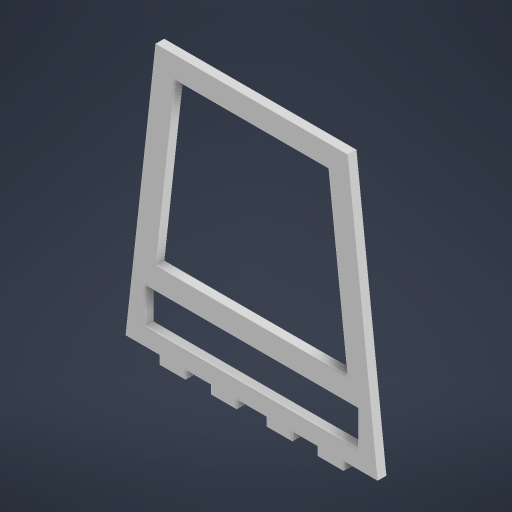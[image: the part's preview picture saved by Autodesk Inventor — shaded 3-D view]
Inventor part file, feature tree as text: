
AUTODESK INVENTOR PART (.ipt)
format: ipt  version: 2023.2 (Build 272271000, 271)  size: 279,040 bytes
history: native  units: mm
features: sketch x2
ambient origin geometry x8: Origin, YZ Plane, XZ Plane, XY Plane, X Axis, Y Axis, Z Axis, Center Point
bodies: Body1 (feature_tree)
feature tree (2):
  sketch  "Sketch1"  dims[d229=90.0mm]
  sketch  "Sketch2"  dims[d232=16.0mm d233=12.0mm d234=12.0mm d235=4.0mm d237=4.0mm d238=0.0mm d239=14.0mm d241=130.0mm d242=100.0mm d243=17.0mm d245=8.0mm d246=10.0mm d247=80.0mm d249=10.0mm d250=4.0mm d251=0.0mm d9=0.5mm d10=0.872665mm d11=0.5mm d12=0.872665mm d13=0.5mm d14=0.872665mm d27=0.5mm d28=0.872665mm d29=0.5mm d30=0.872665mm d88=0.5mm d89=0.872665mm d90=0.5mm d91=0.872665mm d116=0.5mm d117=0.872665mm d118=0.5mm d119=0.872665mm d154=0.5mm d155=0.872665mm d156=0.5mm d157=0.872665mm d181=0.5mm d182=0.872665mm d183=0.5mm d184=0.872665mm d221=0.5mm d222=0.872665mm d223=0.5mm d224=0.872665mm]
